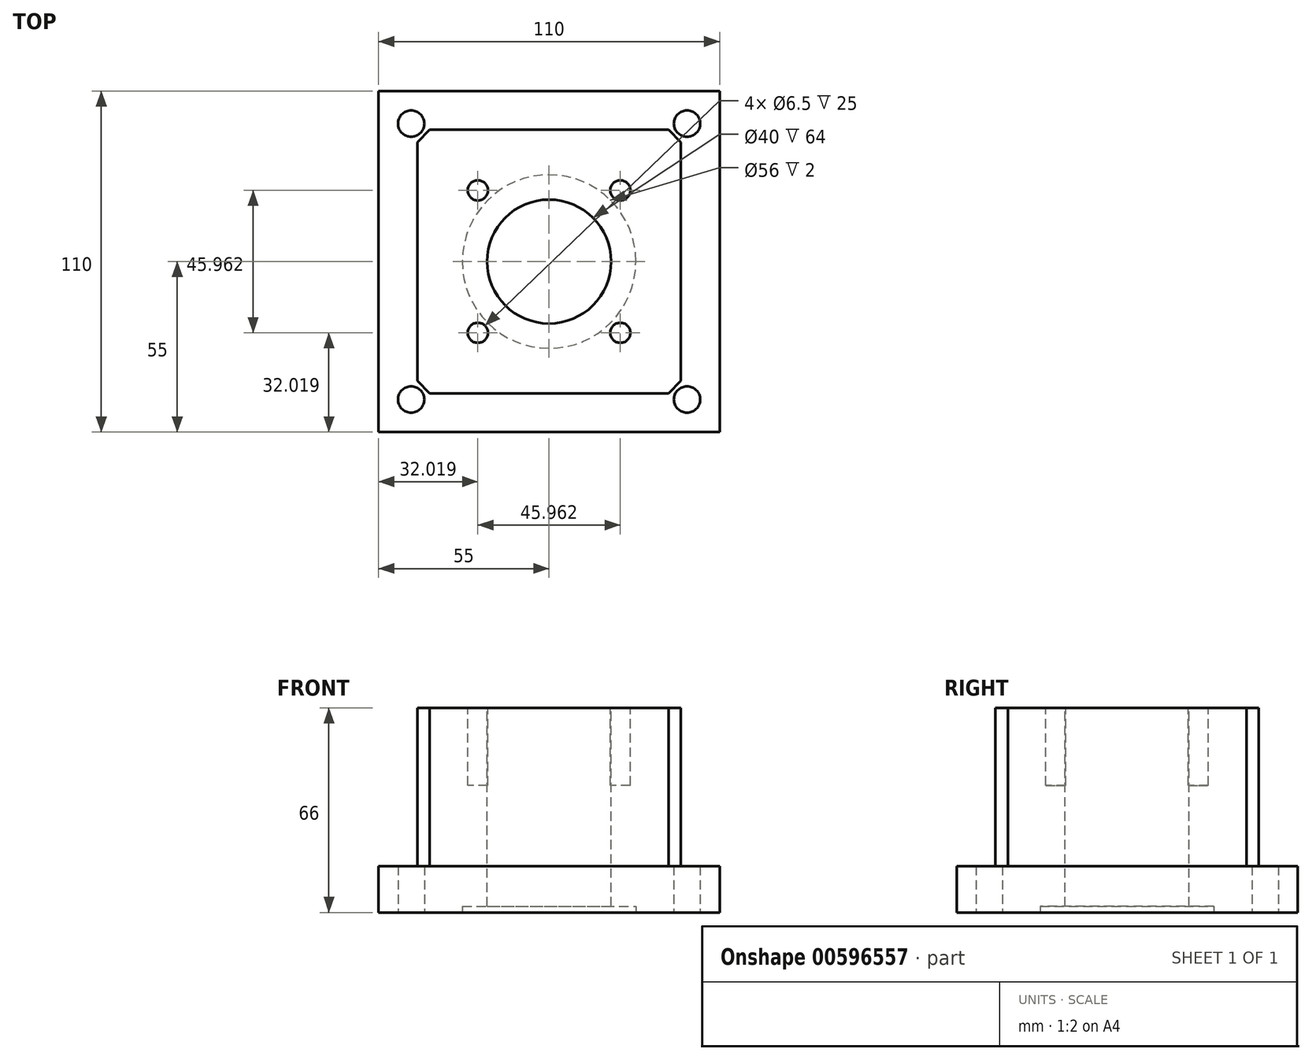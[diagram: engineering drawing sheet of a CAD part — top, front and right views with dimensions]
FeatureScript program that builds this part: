
annotation { "Feature Type Name" : "Feature", "Feature Type Description" : "" }
export const myFeature = defineFeature(function(context is Context, id is Id, definition is map)
    precondition{}
    {
        {
            var Q0;
            Q0=qCreatedBy(makeId("Top.planeOp"),FACE);
            var sketch = newSketch(context, id + "F0", { "sketchPlane" : qUnion([Q0])});
            skLineSegment(sketch, "E0.bottom", {"start": v(0, 0) * mm, "end": v(110, 0) * mm});
            skLineSegment(sketch, "E0.top", {"start": v(0, 110) * mm, "end": v(110, 110) * mm});
            skLineSegment(sketch, "E0.left", {"start": v(0, 0) * mm, "end": v(0, 110) * mm});
            skLineSegment(sketch, "E0.right", {"start": v(110, 0) * mm, "end": v(110, 110) * mm});
            skSolve(sketch);
        }
        {
            var Q0;
            Q0 = qSketchRegion(id + "F0", true);
            extrude(context, id + "F1", {"entities" : qUnion([Q0]), "depth" : 15 * mm, "offsetDistance" : 25 * mm});
        }
        {
            var Q0;
            Q0=makeQuery(id+"F1.opExtrude","CAP_FACE",FACE,{"disambiguationData":[OSD([sQuery(id+"F0.wireOp",EDGE,"E0.bottom"),sQuery(id+"F0.wireOp",EDGE,"E0.top"),sQuery(id+"F0.wireOp",EDGE,"E0.left"),sQuery(id+"F0.wireOp",EDGE,"E0.right")])],"isStart":false});
            var sketch = newSketch(context, id + "F2", { "sketchPlane" : qUnion([Q0])});
            skLineSegment(sketch, "E1.bottom", {"start": v(12.5, 12.5) * mm, "end": v(97.5, 12.5) * mm});
            skLineSegment(sketch, "E1.top", {"start": v(12.5, 97.5) * mm, "end": v(97.5, 97.5) * mm});
            skLineSegment(sketch, "E1.left", {"start": v(12.5, 12.5) * mm, "end": v(12.5, 97.5) * mm});
            skLineSegment(sketch, "E1.right", {"start": v(97.5, 12.5) * mm, "end": v(97.5, 97.5) * mm});
            skSolve(sketch);
        }
        {
            var Q0;
            Q0=makeQuery(id+"F2.imprint","IMPRINT",FACE,{"disambiguationData":[TD([[makeQuery(id+"F2.imprint","IMPRINT",EDGE,{"derivedFrom":sQuery(id+"F2.wireOp",EDGE,"E1.bottom")}),1.0]])]});
            extrude(context, id + "F3", {"entities" : qUnion([Q0]), "operationType" : NewBodyOperationType.ADD, "depth" : 51 * mm, "offsetDistance" : 25 * mm});
        }
        {
            var Q0;
            Q0=makeQuery(id+"F3.opExtrude","SWEPT_EDGE",EDGE,{"disambiguationData":[OSD([sQuery(id+"F2.wireOp",EDGE,"E1.bottom"),sQuery(id+"F2.wireOp",EDGE,"E1.left")])]});
            var Q1;
            Q1=makeQuery(id+"F3.opExtrude","SWEPT_EDGE",EDGE,{"disambiguationData":[OSD([sQuery(id+"F2.wireOp",EDGE,"E1.bottom"),sQuery(id+"F2.wireOp",EDGE,"E1.right")])]});
            var Q2;
            Q2=makeQuery(id+"F3.opExtrude","SWEPT_EDGE",EDGE,{"disambiguationData":[OSD([sQuery(id+"F2.wireOp",EDGE,"E1.top"),sQuery(id+"F2.wireOp",EDGE,"E1.right")])]});
            var Q3;
            Q3=makeQuery(id+"F3.opExtrude","SWEPT_EDGE",EDGE,{"disambiguationData":[OSD([sQuery(id+"F2.wireOp",EDGE,"E1.top"),sQuery(id+"F2.wireOp",EDGE,"E1.left")])]});
            chamfer(context, id + "F4", {"entities" : qUnion([Q0, Q1, Q2, Q3]), "width" : 4 * mm, "tangentPropagation" : true});
        }
        {
            var Q0;
            Q0=makeQuery(id+"F3.opExtrude","CAP_FACE",FACE,{"disambiguationData":[OSD([sQuery(id+"F2.wireOp",EDGE,"E1.bottom"),sQuery(id+"F2.wireOp",EDGE,"E1.top"),sQuery(id+"F2.wireOp",EDGE,"E1.left"),sQuery(id+"F2.wireOp",EDGE,"E1.right")])],"isStart":false});
            var sketch = newSketch(context, id + "F5", { "sketchPlane" : qUnion([Q0])});
            skCircle(sketch, "E2", {"center": v(55, 55) * mm, "radius": 20 * mm});
            skPoint(sketch, "E2.centerSnap0", {"position": v(55, 97.5) * mm});
            skPoint(sketch, "E2.centerSnap1", {"position": v(12.5, 55) * mm});
            skSolve(sketch);
        }
        {
            var Q0;
            Q0=makeQuery(id+"F5.imprint","IMPRINT",FACE,{"disambiguationData":[TD([[makeQuery(id+"F5.imprint","IMPRINT",EDGE,{"derivedFrom":sQuery(id+"F5.wireOp",EDGE,"E2")}),1.0]])]});
            extrude(context, id + "F6", {"entities" : qUnion([Q0]), "operationType" : NewBodyOperationType.REMOVE, "endBound" : BoundingType.THROUGH_ALL, "oppositeDirection" : true, "depth" : 25 * mm, "offsetDistance" : 25 * mm});
        }
        {
            var Q0;
            Q0=makeQuery(id+"F1.opExtrude","CAP_FACE",FACE,{"disambiguationData":[OSD([sQuery(id+"F0.wireOp",EDGE,"E0.bottom"),sQuery(id+"F0.wireOp",EDGE,"E0.top"),sQuery(id+"F0.wireOp",EDGE,"E0.left"),sQuery(id+"F0.wireOp",EDGE,"E0.right")])],"isStart":true});
            var sketch = newSketch(context, id + "F7", { "sketchPlane" : qUnion([Q0])});
            skCircle(sketch, "E3", {"center": v(10.5, -10.5) * mm, "radius": 4.25 * mm});
            skCircle(sketch, "E4.0.1.0", {"center": v(10.5, -99.5) * mm, "radius": 4.25 * mm});
            skCircle(sketch, "E4.1.0.0", {"center": v(99.5, -10.5) * mm, "radius": 4.25 * mm});
            skCircle(sketch, "E4.1.1.0", {"center": v(99.5, -99.5) * mm, "radius": 4.25 * mm});
            skLineSegment(sketch, "E4.direction1", {"start": v(10.5, -10.5) * mm, "end": v(99.5, -10.5) * mm, "construction": true});
            skLineSegment(sketch, "E4.direction2", {"start": v(10.5, -10.5) * mm, "end": v(10.5, -99.5) * mm, "construction": true});
            skSolve(sketch);
        }
        {
            var Q0;
            Q0=makeQuery(id+"F7.imprint","IMPRINT",FACE,{"disambiguationData":[TD([[makeQuery(id+"F7.imprint","IMPRINT",EDGE,{"derivedFrom":sQuery(id+"F7.wireOp",EDGE,"E3")}),1.0]])]});
            var Q1;
            Q1=makeQuery(id+"F7.imprint","IMPRINT",FACE,{"disambiguationData":[TD([[makeQuery(id+"F7.imprint","IMPRINT",EDGE,{"derivedFrom":sQuery(id+"F7.wireOp",EDGE,"E4.1.0.0")}),1.0]])]});
            var Q2;
            Q2=makeQuery(id+"F7.imprint","IMPRINT",FACE,{"disambiguationData":[TD([[makeQuery(id+"F7.imprint","IMPRINT",EDGE,{"derivedFrom":sQuery(id+"F7.wireOp",EDGE,"E4.1.1.0")}),1.0]])]});
            var Q3;
            Q3=makeQuery(id+"F7.imprint","IMPRINT",FACE,{"disambiguationData":[TD([[makeQuery(id+"F7.imprint","IMPRINT",EDGE,{"derivedFrom":sQuery(id+"F7.wireOp",EDGE,"E4.0.1.0")}),1.0]])]});
            extrude(context, id + "F8", {"entities" : qUnion([Q0, Q1, Q2, Q3]), "operationType" : NewBodyOperationType.REMOVE, "endBound" : BoundingType.THROUGH_ALL, "oppositeDirection" : true, "depth" : 25 * mm, "offsetDistance" : 25 * mm});
        }
        {
            var Q0;
            Q0=makeQuery(id+"F1.opExtrude","CAP_FACE",FACE,{"disambiguationData":[OSD([sQuery(id+"F0.wireOp",EDGE,"E0.bottom"),sQuery(id+"F0.wireOp",EDGE,"E0.top"),sQuery(id+"F0.wireOp",EDGE,"E0.left"),sQuery(id+"F0.wireOp",EDGE,"E0.right")])],"isStart":true});
            var sketch = newSketch(context, id + "F9", { "sketchPlane" : qUnion([Q0])});
            skCircle(sketch, "E5", {"center": v(55, -55) * mm, "radius": 28 * mm});
            skSolve(sketch);
        }
        {
            var Q0;
            Q0 = qSketchRegion(id + "F9", true);
            extrude(context, id + "F10", {"entities" : qUnion([Q0]), "operationType" : NewBodyOperationType.REMOVE, "oppositeDirection" : true, "depth" : 2 * mm, "offsetDistance" : 25 * mm});
        }
        {
            var Q0;
            Q0=makeQuery(id+"F3.opExtrude","CAP_FACE",FACE,{"disambiguationData":[OSD([sQuery(id+"F2.wireOp",EDGE,"E1.bottom"),sQuery(id+"F2.wireOp",EDGE,"E1.top"),sQuery(id+"F2.wireOp",EDGE,"E1.left"),sQuery(id+"F2.wireOp",EDGE,"E1.right")])],"isStart":false});
            var sketch = newSketch(context, id + "F11", { "sketchPlane" : qUnion([Q0])});
            skCircle(sketch, "E6", {"center": v(55, 55) * mm, "radius": 32.5 * mm, "construction": true});
            skLineSegment(sketch, "E7", {"start": v(32.02, 77.98) * mm, "end": v(55, 55) * mm});
            skCircle(sketch, "E8", {"center": v(32.02, 77.98) * mm, "radius": 3.25 * mm});
            skCircle(sketch, "E9.1.0", {"center": v(32.02, 32.02) * mm, "radius": 3.25 * mm});
            skCircle(sketch, "E9.2.0", {"center": v(77.98, 32.02) * mm, "radius": 3.25 * mm});
            skCircle(sketch, "E9.3.0", {"center": v(77.98, 77.98) * mm, "radius": 3.25 * mm});
            skLineSegment(sketch, "E10", {"start": v(55, 55) * mm, "end": v(55, 87.5) * mm, "construction": true});
            skSolve(sketch);
        }
        {
            var Q0;
            Q0=makeQuery(id+"F11.imprint","IMPRINT",FACE,{"disambiguationData":[TD([[makeQuery(id+"F11.imprint","IMPRINT",EDGE,{"derivedFrom":sQuery(id+"F11.wireOp",EDGE,"E8")}),1.0]])]});
            var Q1;
            Q1=makeQuery(id+"F11.imprint","IMPRINT",FACE,{"disambiguationData":[TD([[makeQuery(id+"F11.imprint","IMPRINT",EDGE,{"derivedFrom":sQuery(id+"F11.wireOp",EDGE,"E9.3.0")}),1.0]])]});
            var Q2;
            Q2=makeQuery(id+"F11.imprint","IMPRINT",FACE,{"disambiguationData":[TD([[makeQuery(id+"F11.imprint","IMPRINT",EDGE,{"derivedFrom":sQuery(id+"F11.wireOp",EDGE,"E9.2.0")}),1.0]])]});
            var Q3;
            Q3=makeQuery(id+"F11.imprint","IMPRINT",FACE,{"disambiguationData":[TD([[makeQuery(id+"F11.imprint","IMPRINT",EDGE,{"derivedFrom":sQuery(id+"F11.wireOp",EDGE,"E9.1.0")}),1.0]])]});
            extrude(context, id + "F12", {"entities" : qUnion([Q0, Q1, Q2, Q3]), "operationType" : NewBodyOperationType.REMOVE, "oppositeDirection" : true, "depth" : 25 * mm, "offsetDistance" : 25 * mm});
        }
    });
